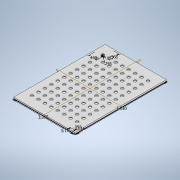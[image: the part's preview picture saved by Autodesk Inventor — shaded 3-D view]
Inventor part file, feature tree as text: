
AUTODESK INVENTOR PART (.ipt)
format: ipt  version: 2020 (Build 240168000, 168)  size: 337,408 bytes
history: native  units: in
note: dims shown in document units (in); Inventor stores cm internally (conversion verified against a paired STEP export)
features: extrude x3, sketch x2, plane x2, mirror x2, hole x1, pattern_linear x1
ambient origin geometry x8: Origin, YZ Plane, XZ Plane, XY Plane, X Axis, Y Axis, Z Axis, Center Point
bodies: Solid1 (feature_tree)
feature tree (11):
  sketch  "Sketch1"  dims[d0=3.365in d1=5.03in]
  extrude  "Extrusion1"  Depth=5.03in
  hole  "Hole1"  [1 undecoded]
  extrude  "Extrusion2"  Depth=0.0787in
  pattern_linear  "Rectangular Pattern1"  Spacing1=0.2756in  [1 undecoded]
  plane  "Work Plane1"
  plane  "Work Plane2"
  extrude  "Extrusion3"  Depth=0.0787in
  mirror  "Mirror1"
  mirror  "Mirror2"
  sketch  "Sketch2"  dims[d2=0.0787in d3=0.0in d4=0.4425in d5=0.5661in d6=0.2756in d7=0.1575in d8=0.75in d9=0.37in d10=0.25in d11=90.0deg d12=0.75in d13=0.0in d14=3.1496in d16=0.3543in d17=4.7244in d19=0.3543in d20=0.1875in d21=0.1875in d29=0.443in d30=0.566in d31=0.2953in d32=0.1575in d33=0.0394in d34=0.0in d35=0.0984in d36=0.0787in d37=0.0in d38=0.0344in]
note: 2 required parameter values undecoded (feature->parameter linkage not recoverable at this tier; creation-order binding heuristic only, values carry confidence <= 0.55)
